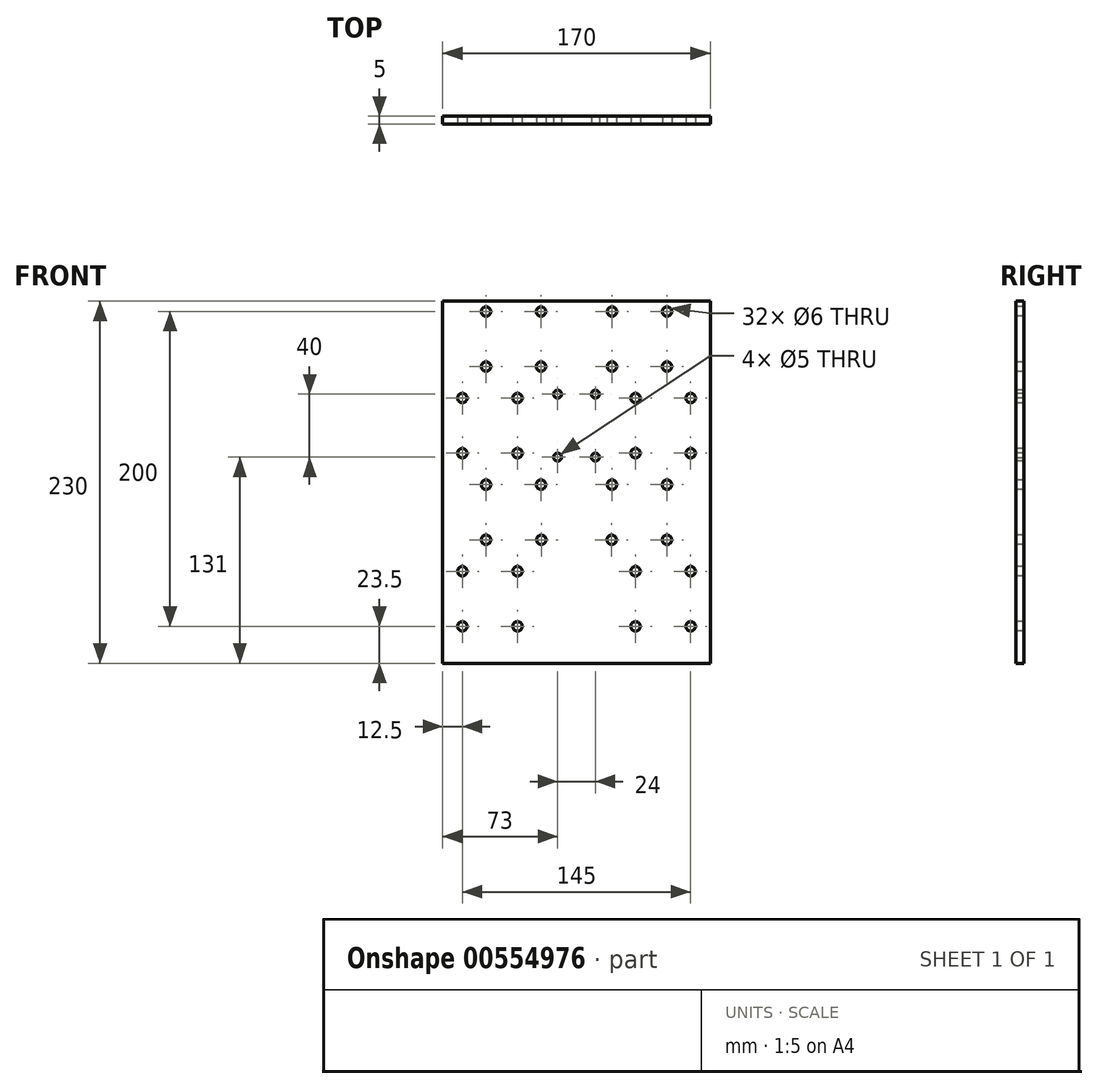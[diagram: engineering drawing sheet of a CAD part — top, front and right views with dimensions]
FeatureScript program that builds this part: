
annotation { "Feature Type Name" : "Feature", "Feature Type Description" : "" }
export const myFeature = defineFeature(function(context is Context, id is Id, definition is map)
    precondition{}
    {
        {
            var Q0;
            Q0=qCreatedBy(makeId("Front.planeOp"),FACE);
            var sketch = newSketch(context, id + "F0", { "sketchPlane" : qUnion([Q0])});
            skLineSegment(sketch, "E0.bottom", {"start": v(85, 115) * mm, "end": v(-85, 115) * mm});
            skLineSegment(sketch, "E0.top", {"start": v(85, -115) * mm, "end": v(-85, -115) * mm});
            skLineSegment(sketch, "E0.left", {"start": v(85, 115) * mm, "end": v(85, -115) * mm});
            skLineSegment(sketch, "E0.right", {"start": v(-85, 115) * mm, "end": v(-85, -115) * mm});
            skPoint(sketch, "E0.middle", {"position": v(0, 0) * mm});
            skSolve(sketch);
        }
        {
            var Q0;
            Q0 = qSketchRegion(id + "F0", true);
            extrude(context, id + "F1", {"entities" : qUnion([Q0]), "depth" : 5 * mm, "offsetDistance" : 25 * mm});
        }
        {
            var Q0;
            Q0=makeQuery(id+"F1.opExtrude","CAP_FACE",FACE,{"disambiguationData":[OSD([sQuery(id+"F0.wireOp",EDGE,"E0.bottom"),sQuery(id+"F0.wireOp",EDGE,"E0.top"),sQuery(id+"F0.wireOp",EDGE,"E0.left"),sQuery(id+"F0.wireOp",EDGE,"E0.right")])],"isStart":false});
            var sketch = newSketch(context, id + "F2", { "sketchPlane" : qUnion([Q0])});
            skCircle(sketch, "E1", {"center": v(-57.5, 108.5) * mm, "radius": 3 * mm});
            skCircle(sketch, "E2", {"center": v(-22.5, 108.5) * mm, "radius": 3 * mm});
            skCircle(sketch, "E3", {"center": v(-57.5, 73.5) * mm, "radius": 3 * mm});
            skCircle(sketch, "E4", {"center": v(-22.5, 73.5) * mm, "radius": 3 * mm});
            skCircle(sketch, "E5.MirrorC", {"center": v(22.5, 108.5) * mm, "radius": 3 * mm});
            skCircle(sketch, "E6.MirrorC", {"center": v(22.5, 73.5) * mm, "radius": 3 * mm});
            skCircle(sketch, "E7.MirrorC", {"center": v(57.5, 73.5) * mm, "radius": 3 * mm});
            skCircle(sketch, "E8.MirrorC", {"center": v(57.5, 108.5) * mm, "radius": 3 * mm});
            skCircle(sketch, "E9", {"center": v(57.5, -1.5) * mm, "radius": 3 * mm});
            skCircle(sketch, "E10", {"center": v(22.5, -1.5) * mm, "radius": 3 * mm});
            skCircle(sketch, "E11", {"center": v(22.35, -36.5) * mm, "radius": 3 * mm});
            skCircle(sketch, "E12", {"center": v(57.5, -36.5) * mm, "radius": 3 * mm});
            skCircle(sketch, "E13.MirrorC", {"center": v(-22.5, -1.5) * mm, "radius": 3 * mm});
            skCircle(sketch, "E14.MirrorC", {"center": v(-57.5, -1.5) * mm, "radius": 3 * mm});
            skCircle(sketch, "E15.MirrorC", {"center": v(-22.35, -36.5) * mm, "radius": 3 * mm});
            skCircle(sketch, "E16.MirrorC", {"center": v(-57.5, -36.5) * mm, "radius": 3 * mm});
            skSolve(sketch);
        }
        {
            var Q0;
            Q0 = qSketchRegion(id + "F2", true);
            extrude(context, id + "F3", {"entities" : qUnion([Q0]), "operationType" : NewBodyOperationType.REMOVE, "oppositeDirection" : true, "depth" : 5 * mm, "offsetDistance" : 25 * mm});
        }
        {
            var Q0;
            Q0=makeQuery(id+"F1.opExtrude","CAP_FACE",FACE,{"disambiguationData":[OSD([sQuery(id+"F0.wireOp",EDGE,"E0.bottom"),sQuery(id+"F0.wireOp",EDGE,"E0.top"),sQuery(id+"F0.wireOp",EDGE,"E0.left"),sQuery(id+"F0.wireOp",EDGE,"E0.right")])],"isStart":false});
            var sketch = newSketch(context, id + "F4", { "sketchPlane" : qUnion([Q0])});
            skCircle(sketch, "E17", {"center": v(-12, 56) * mm, "radius": 2.5 * mm});
            skCircle(sketch, "E18", {"center": v(-12, 16) * mm, "radius": 2.5 * mm});
            skCircle(sketch, "E19", {"center": v(12, 56) * mm, "radius": 2.5 * mm});
            skCircle(sketch, "E20", {"center": v(12, 16) * mm, "radius": 2.5 * mm});
            skSolve(sketch);
        }
        {
            var Q0;
            Q0 = qSketchRegion(id + "F4", true);
            extrude(context, id + "F5", {"entities" : qUnion([Q0]), "operationType" : NewBodyOperationType.REMOVE, "oppositeDirection" : true, "depth" : 5 * mm, "offsetDistance" : 25 * mm});
        }
        {
            var Q0;
            Q0=makeQuery(id+"F1.opExtrude","CAP_FACE",FACE,{"disambiguationData":[OSD([sQuery(id+"F0.wireOp",EDGE,"E0.bottom"),sQuery(id+"F0.wireOp",EDGE,"E0.top"),sQuery(id+"F0.wireOp",EDGE,"E0.left"),sQuery(id+"F0.wireOp",EDGE,"E0.right")])],"isStart":false});
            var sketch = newSketch(context, id + "F6", { "sketchPlane" : qUnion([Q0])});
            skCircle(sketch, "E21", {"center": v(37.5, 53.5) * mm, "radius": 3 * mm});
            skCircle(sketch, "E22", {"center": v(72.5, 53.5) * mm, "radius": 3 * mm});
            skCircle(sketch, "E23", {"center": v(37.5, 18.5) * mm, "radius": 3 * mm});
            skCircle(sketch, "E24", {"center": v(72.5, 18.5) * mm, "radius": 3 * mm});
            skPoint(sketch, "E25.start.orphan", {"position": v(12, 36) * mm});
            skPoint(sketch, "E26.orphan", {"position": v(12, 56) * mm});
            skPoint(sketch, "E27.end.orphan", {"position": v(12, 16) * mm});
            skLineSegment(sketch, "E28", {"start": v(37.5, 53.5) * mm, "end": v(40.5, 53.5) * mm});
            skLineSegment(sketch, "E29.trimOffspring", {"start": v(69.5, 53.5) * mm, "end": v(72.5, 53.5) * mm});
            skPoint(sketch, "E30.start.orphan", {"position": v(55, 53.5) * mm});
            skCircle(sketch, "E31.MirrorC", {"center": v(-37.5, 53.5) * mm, "radius": 3 * mm});
            skCircle(sketch, "E32.MirrorC", {"center": v(-72.5, 53.5) * mm, "radius": 3 * mm});
            skCircle(sketch, "E33.MirrorC", {"center": v(-37.5, 18.5) * mm, "radius": 3 * mm});
            skCircle(sketch, "E34.MirrorC", {"center": v(-72.5, 18.5) * mm, "radius": 3 * mm});
            skSolve(sketch);
        }
        {
            var Q0;
            Q0 = qSketchRegion(id + "F6", true);
            extrude(context, id + "F7", {"entities" : qUnion([Q0]), "operationType" : NewBodyOperationType.REMOVE, "oppositeDirection" : true, "depth" : 5 * mm, "offsetDistance" : 25 * mm});
        }
        {
            var Q0;
            Q0=makeQuery(id+"F1.opExtrude","CAP_FACE",FACE,{"disambiguationData":[OSD([sQuery(id+"F0.wireOp",EDGE,"E0.bottom"),sQuery(id+"F0.wireOp",EDGE,"E0.top"),sQuery(id+"F0.wireOp",EDGE,"E0.left"),sQuery(id+"F0.wireOp",EDGE,"E0.right")])],"isStart":false});
            var sketch = newSketch(context, id + "F8", { "sketchPlane" : qUnion([Q0])});
            skCircle(sketch, "E35", {"center": v(-37.5, -56.5) * mm, "radius": 3 * mm});
            skCircle(sketch, "E36", {"center": v(-72.5, -56.5) * mm, "radius": 3 * mm});
            skCircle(sketch, "E37", {"center": v(-37.5, -91.5) * mm, "radius": 3 * mm});
            skCircle(sketch, "E38", {"center": v(-72.5, -91.5) * mm, "radius": 3 * mm});
            skPoint(sketch, "E39.startSnap0", {"position": v(-55, -74) * mm});
            skPoint(sketch, "E40.orphan", {"position": v(-55, -56.5) * mm});
            skPoint(sketch, "E41.end.orphan", {"position": v(-55, -91.5) * mm});
            skPoint(sketch, "E39.end.orphan", {"position": v(-55, -74) * mm});
            skPoint(sketch, "E39.start.orphan", {"position": v(-61.18, -74) * mm});
            skCircle(sketch, "E42.MirrorC", {"center": v(37.5, -56.5) * mm, "radius": 3 * mm});
            skCircle(sketch, "E43.MirrorC", {"center": v(72.5, -56.5) * mm, "radius": 3 * mm});
            skCircle(sketch, "E44.MirrorC", {"center": v(37.5, -91.5) * mm, "radius": 3 * mm});
            skCircle(sketch, "E45.MirrorC", {"center": v(72.5, -91.5) * mm, "radius": 3 * mm});
            skSolve(sketch);
        }
        {
            var Q0;
            Q0 = qSketchRegion(id + "F8", true);
            extrude(context, id + "F9", {"entities" : qUnion([Q0]), "operationType" : NewBodyOperationType.REMOVE, "oppositeDirection" : true, "depth" : 5 * mm, "offsetDistance" : 25 * mm});
        }
    });
